# Revit family: Luminaria DECO HORIZON
name_source: partatom
category: Luminarias
revit_build: Autodesk Revit 2016 (Build: 20150220_1215(x64)
units: mm (PartAtom-declared; Revit-internal decimal feet)

## family parameters
Compartido = No
Corte con vacíos al cargar = No
Cota de conector redondo = Diámetro de uso
Número OmniClass = 23.80.70.00
Origen de luz = Sí
Punto de cálculo de habitación = No
Se basa en plano de trabajo = No
Siempre vertical = No
Tipo de pieza = Normal
Título OmniClass = Lighting

## types (1)
- DECO HORIZON 48LED 700 mA 106W 4000K T3
    Ajuste de potencia = Si
    Alto = 135 mm
    Altura columna = 4-8 m
    Archivo de red fotométrica = ILDH04833_DECOHORIZON48LED700mA106W3000KT3-2685.ies
    Cambio de temperatura de color de luz atenuada = <Ninguno>
    Carga aparente = 0 VA
    Certificaciones = CE, ENEC, AENOR, CB SCHEME, RETILAP.
    Clase de aislamiento = Clase I / Clase II
    Classificación = Iluminación
    Comentarios de tipo = Deco Horizon pertenece a la completa familia Essentials y ofrece funcionalidad y un diseño técnicamente imepcable.Pefecta para instalar en columnas de 4 a 8 metros.
    Comentarios de vataje = 1
    Descripción = Diseño Essentials.Excelente disipación térmica.Disipación pasiva sin aletas.Compartimeinto de driver separado de la placa LED para mejorar el aislamiento térmico entre ellos.Diseño con antideslumbramiento.Aperutra sin herramientas.Facil instalación.Fijación en tubo de Ø 60 mm tanto en top como en Laterial.
    Diametro fijación = Ø 60 mm tanto en top como en lateral
    Difusor = Cristal
    Diámetro = 450 mm
    Diámetro de círculo de emisión = 400 mm
    Driver = Incluido
    Fabricante = BENITO
    Ficha tecnica = http://www.benito.com
    Filtro de color = 16777215
    Forma visible en renderización = No
    Frequencia nominal = 50/60 Hz
    Indice de reproducción cromatica = >70
    Instrucciones de montaje = http://www.benito.com
    Lámpara = Led
    Material cuerpo = Aluminio
    Modelo = DECO HORIZON 48 LED 700 mA 106W 4000K T3
    Peso = 7,5 Kg
    Protección IP = 66
    Protección impacto IK = 09
    Referencia = ILDH
    Regulable = Si
    Sistema regulable = SI
    Tipo de opticas = T2,T3,T4
    URL = http://www.benito.com
    URL producto = http://www.benito.com
    Voltage nominal = 220-240 V AC
    Ángulo de inclinación = 90.00°

## geometry (parser evidence)
native form markers: Blend x4
no freeform markers — native parametric forms only
